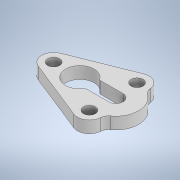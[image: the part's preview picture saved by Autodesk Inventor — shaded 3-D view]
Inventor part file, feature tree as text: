
AUTODESK INVENTOR PART (.ipt)
format: ipt  version: 2021 (Build 250183000, 183)  size: 151,040 bytes
history: native  units: mm
features: extrude x1, sketch x1
ambient origin geometry x8: Origin, YZ Plane, XZ Plane, XY Plane, X Axis, Y Axis, Z Axis, Center Point
bodies: Solid1 (feature_tree)
feature tree (2):
  extrude  "Extrusion1"  TaperAngle=0.0deg  [1 undecoded]
  sketch  "Sketch1"  dims[d0=50.0mm d1=0.0mm d2=20.0mm d3=20.0mm d4=20.0mm d5=40.0mm d6=20.0mm d7=10.0mm d8=10.0mm d9=10.0mm d10=12.0mm d11=30.0mm d12=6.0mm d13=0.0mm d14=22.0mm d15=38.0mm d16=7.0mm d17=7.0mm d18=2.0mm d19=10.0mm d20=0.0mm]
note: 1 required parameter value undecoded (feature->parameter linkage not recoverable at this tier; creation-order binding heuristic only, values carry confidence <= 0.55)
